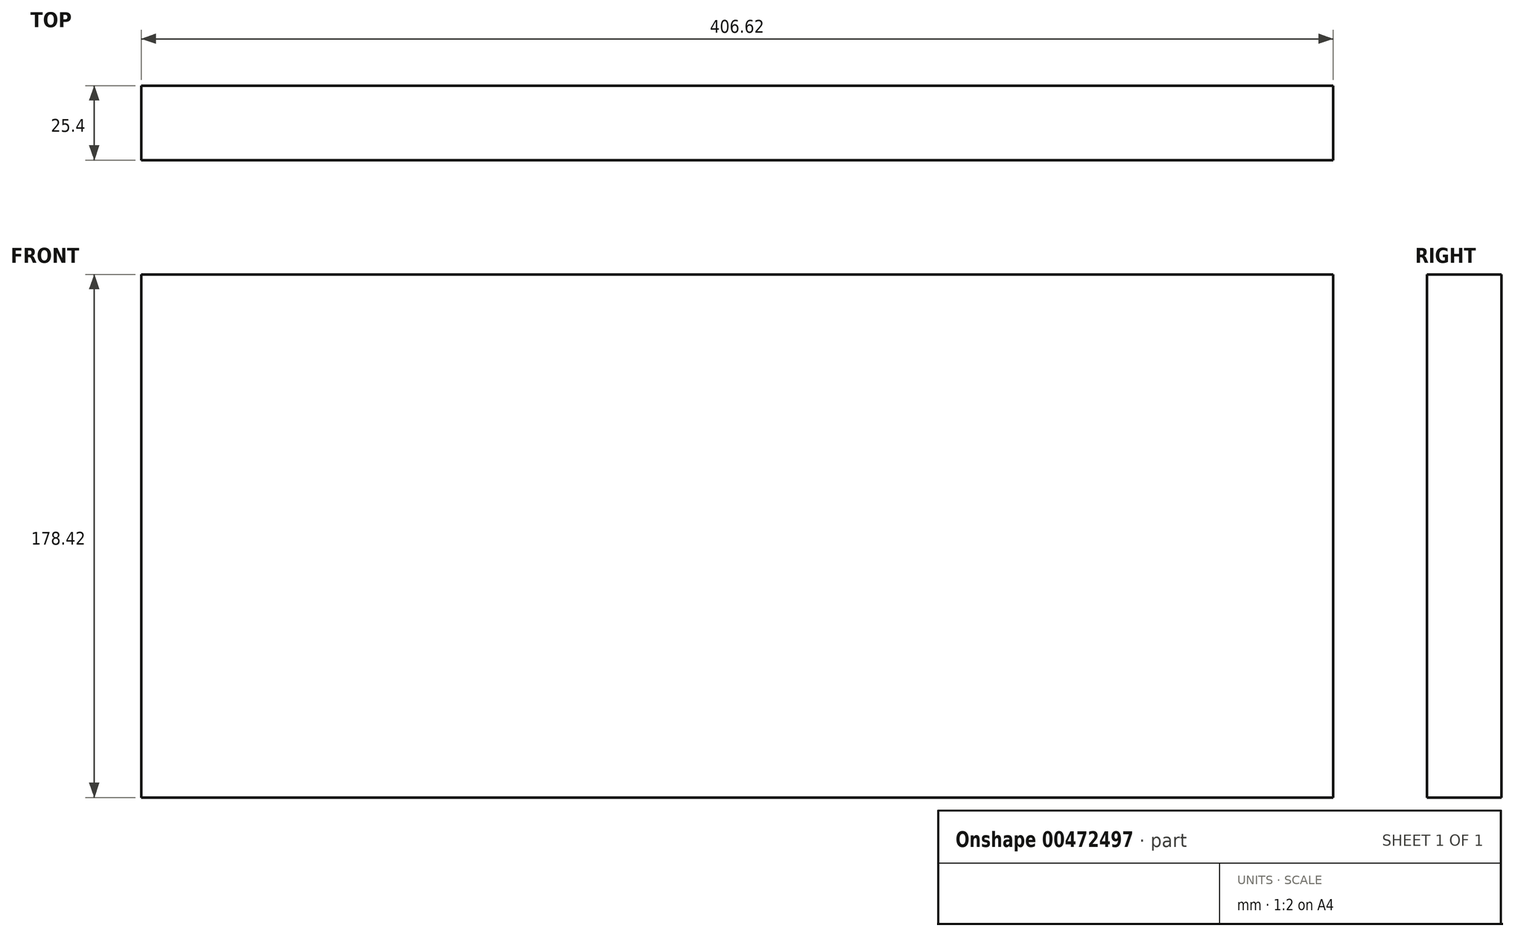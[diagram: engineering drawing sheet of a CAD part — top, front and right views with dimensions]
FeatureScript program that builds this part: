
annotation { "Feature Type Name" : "Feature", "Feature Type Description" : "" }
export const myFeature = defineFeature(function(context is Context, id is Id, definition is map)
    precondition{}
    {
        {
            var Q0;
            Q0=qCreatedBy(makeId("Front.planeOp"),FACE);
            var sketch = newSketch(context, id + "F0", { "sketchPlane" : qUnion([Q0])});
            skLineSegment(sketch, "E0.bottom", {"start": v(-142.37, -45.58) * mm, "end": v(264.25, -45.58) * mm});
            skLineSegment(sketch, "E0.top", {"start": v(-142.37, 132.84) * mm, "end": v(264.25, 132.84) * mm});
            skLineSegment(sketch, "E0.left", {"start": v(-142.37, -45.58) * mm, "end": v(-142.37, 132.84) * mm});
            skLineSegment(sketch, "E0.right", {"start": v(264.25, -45.58) * mm, "end": v(264.25, 132.84) * mm});
            skPoint(sketch, "E0.middle", {"position": v(60.94, 43.63) * mm});
            skSolve(sketch);
        }
        {
            var Q0;
            Q0=makeQuery(id+"F0.imprint","IMPRINT",FACE,{"disambiguationData":[TD([[makeQuery(id+"F0.imprint","IMPRINT",EDGE,{"derivedFrom":sQuery(id+"F0.wireOp",EDGE,"E0.bottom")}),1.0]])]});
            var Q1;
            Q1 = qSketchRegion(id + "F0", true);
            extrude(context, id + "F1", {"entities" : qUnion([Q0, Q1]), "depth" : 25.4 * mm});
        }
    });
